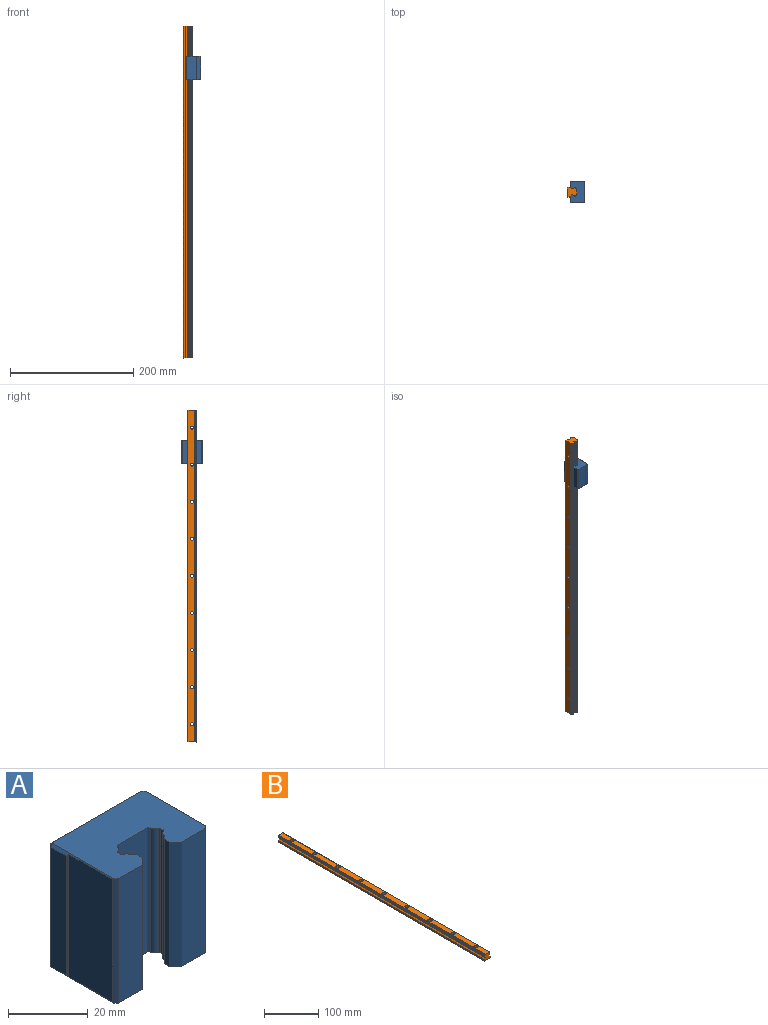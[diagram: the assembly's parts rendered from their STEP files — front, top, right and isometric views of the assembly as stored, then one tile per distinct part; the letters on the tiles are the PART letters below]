
ASSEMBLY  parts=2 mates=1
PART A: 58 faces, bbox 34x23.5x38.2 mm
  f0: plane 3.25x3.25mm, normal (0,1,0), area 8.3mm2, adj f14
  f1: plane 3.25x3.25mm, normal (0,1,0), area 8.3mm2, adj f15
  f2: plane 3.25x3.25mm, normal (0,1,0), area 8.3mm2, adj f18
  f3: plane 3.25x3.25mm, normal (0,1,0), area 8.3mm2, adj f19
  f4: plane 37.7x0.5mm, normal (-0.62,-0.78,0), area 23.8mm2, adj f8,f23,f24,f42
  f5: plane 38.2x0.92mm, normal (1,0,0), area 35.1mm2, adj f26,f28,f34,f57
  f6: plane 38.2x0.92mm, normal (-1,0,0), area 35.1mm2, adj f30,f32,f34,f57
  f7: plane 1.31x1.31mm, normal (-0.5,0.5,-0.71), area 1.2mm2, adj f8,f17,f21,f34
  f8: plane 21.75x0.75mm, normal (-0.71,0,-0.71), area 11.6mm2, adj f4,f7,f23,f24,f25,f34
  f9: plane 1.31x1.31mm, normal (0.5,0.5,-0.71), area 1.2mm2, adj f11,f12,f21,f34
  f10: plane 37.7x0.5mm, normal (0.62,-0.78,0), area 23.8mm2, adj f11,f36,f37,f54
  f11: plane 21.75x0.75mm, normal (0.71,0,-0.71), area 11.6mm2, adj f9,f10,f34,f35,f36,f37
  f12: plane 36.7x1mm, normal (0.71,0.71,0), area 51.9mm2, adj f9,f37,f38,f55
  f13: plane 37.51x0.41mm, normal (-0.71,0.71,0), area 21.4mm2, adj f20,f21,f38,f56
  f14: cylinder r=1.62mm len=15mm, axis (0,-1,0), area 153.2mm2, adj f0,f38
  f15: cylinder r=1.62mm len=15mm, axis (0,-1,0), area 153.2mm2, adj f1,f38
  f16: plane 37.51x0.41mm, normal (0.71,0.71,0), area 21.4mm2, adj f21,f22,f39,f56
  f17: plane 36.7x1mm, normal (-0.71,0.71,0), area 51.9mm2, adj f7,f24,f39,f41
  f18: cylinder r=1.62mm len=15mm, axis (0,-1,0), area 153.2mm2, adj f2,f39
  f19: cylinder r=1.62mm len=15mm, axis (0,-1,0), area 153.2mm2, adj f3,f39
  f20: cylinder r=1mm len=38.1mm, axis (0,0,-1), area 29.8mm2, adj f13,f21,f40,f56
  f21: plane 32x0.75mm, normal (0,0.71,-0.71), area 23mm2, adj f7,f9,f13,f16,f20,f22,f34,f38
  f22: cylinder r=1mm len=38.1mm, axis (0,0,-1), area 29.8mm2, adj f16,f21,f40,f56
  f23: plane 37.7x15.5mm, normal (-1,0,0), area 584.3mm2, adj f4,f8,f25,f42
  f24: plane 36.7x5.6mm, normal (-1,0,0), area 205.5mm2, adj f4,f8,f17,f42
  f25: plane 38.2x1mm, normal (-0.71,-0.71,0), area 53.9mm2, adj f8,f23,f34,f42,f43,f57
  f26: cylinder r=0.5mm len=38.2mm, axis (0,0,-1), area 25mm2, adj f5,f34,f46,f57
  f27: plane 38.2x1.09mm, normal (0.68,0.74,0), area 56.3mm2, adj f34,f45,f46,f57
  f28: cylinder r=0.5mm len=38.2mm, axis (0,0,-1), area 25mm2, adj f5,f34,f47,f57
  f29: plane 38.2x0.5mm, normal (0.71,-0.71,0), area 26.8mm2, adj f34,f47,f48,f57
  f30: cylinder r=0.5mm len=38.2mm, axis (0,0,-1), area 25mm2, adj f6,f34,f49,f57
  f31: plane 38.2x0.5mm, normal (-0.71,-0.71,0), area 26.8mm2, adj f34,f48,f49,f57
  f32: cylinder r=0.5mm len=38.2mm, axis (0,0,-1), area 25mm2, adj f6,f34,f50,f57
  f33: plane 38.2x1.09mm, normal (-0.68,0.74,0), area 56.3mm2, adj f34,f50,f51,f57
  f34: plane 32.5x22.75mm, normal (0,0,-1), area 612.7mm2, adj f5,f6,f7,f8,f9,f11,f21,f25
  f35: plane 38.2x1mm, normal (0.71,-0.71,0), area 53.9mm2, adj f11,f34,f36,f53,f54,f57
  f36: plane 37.7x15.5mm, normal (1,0,0), area 584.3mm2, adj f10,f11,f35,f54
  f37: plane 36.7x5.6mm, normal (1,0,0), area 205.5mm2, adj f10,f11,f12,f54
  f38: plane 36.7x10.25mm, normal (0,1,0), area 359.6mm2, adj f12,f13,f14,f15,f21,f56
  f39: plane 36.7x10.25mm, normal (0,1,0), area 359.6mm2, adj f16,f17,f18,f19,f21,f56
  f40: plane 38.1x9.27mm, normal (0,1,0), area 353.2mm2, adj f20,f21,f22,f56
  f41: plane 1.31x1.31mm, normal (-0.5,0.5,0.71), area 1.2mm2, adj f17,f42,f56,f57
  f42: plane 21.75x0.75mm, normal (-0.71,0,0.71), area 11.6mm2, adj f4,f23,f24,f25,f41,f57
  f43: plane 38.2x8.54mm, normal (0,-1,0), area 326.2mm2, adj f25,f34,f44,f57
  f44: plane 38.2x2.16mm, normal (0.68,-0.73,0), area 112.5mm2, adj f34,f43,f45,f57
  f45: plane 38.2x2mm, normal (1,0,0), area 76.4mm2, adj f27,f34,f44,f57
  f46: cylinder r=1.67mm len=38.2mm, axis (0,0,-1), area 81.4mm2, adj f26,f27,f34,f57
  f47: cylinder r=1.67mm len=38.2mm, axis (0,0,-1), area 81.4mm2, adj f28,f29,f34,f57
  f48: plane 38.2x10.78mm, normal (0,-1,0), area 411.8mm2, adj f29,f31,f34,f57
  f49: cylinder r=1.67mm len=38.2mm, axis (0,0,-1), area 81.4mm2, adj f30,f31,f34,f57
  f50: cylinder r=1.67mm len=38.2mm, axis (0,0,-1), area 81.4mm2, adj f32,f33,f34,f57
  f51: plane 38.2x2mm, normal (-1,0,0), area 76.4mm2, adj f33,f34,f52,f57
  f52: plane 38.2x2.16mm, normal (-0.68,-0.73,0), area 112.5mm2, adj f34,f51,f53,f57
  f53: plane 38.2x8.54mm, normal (0,-1,0), area 326.2mm2, adj f34,f35,f52,f57
  f54: plane 21.75x0.75mm, normal (0.71,0,0.71), area 11.6mm2, adj f10,f35,f36,f37,f55,f57
  f55: plane 1.31x1.31mm, normal (0.5,0.5,0.71), area 1.2mm2, adj f12,f54,f56,f57
  f56: plane 32x0.75mm, normal (0,0.71,0.71), area 23mm2, adj f13,f16,f20,f22,f38,f39,f40,f41
  f57: plane 32.5x22.75mm, normal (0,0,1), area 612.7mm2, adj f5,f6,f25,f26,f27,f28,f29,f30
PART B: 55 faces, bbox 15x538x15 mm
  f0: plane 538x0.92mm, normal (1,0,0), area 496.6mm2, adj f4,f5,f42,f44
  f1: plane 538x0.92mm, normal (-1,0,0), area 496.6mm2, adj f8,f9,f42,f44
  f2: plane 538x1mm, normal (0.71,0,-0.71), area 760.8mm2, adj f20,f21,f42,f44
  f3: plane 538x1.09mm, normal (0.68,0,-0.74), area 796.4mm2, adj f23,f24,f42,f44
  f4: cylinder r=0.45mm len=538mm, axis (0,-1,0), area 317.5mm2, adj f0,f24,f42,f44
  f5: cylinder r=0.45mm len=538mm, axis (0,-1,0), area 317.5mm2, adj f0,f25,f42,f44
  f6: plane 538x0.47mm, normal (0.71,0,0.71), area 358.8mm2, adj f25,f26,f42,f44
  f7: plane 538x0.47mm, normal (-0.71,0,0.71), area 358.8mm2, adj f26,f27,f42,f44
  f8: cylinder r=0.45mm len=538mm, axis (0,-1,0), area 317.5mm2, adj f1,f27,f42,f44
  f9: cylinder r=0.45mm len=538mm, axis (0,-1,0), area 317.5mm2, adj f1,f28,f42,f44
  f10: plane 538x1.09mm, normal (-0.68,0,-0.74), area 796.4mm2, adj f28,f29,f42,f44
  f11: cylinder r=3.75mm len=7.5mm, axis (0,0,-1), area 129.6mm2, adj f26,f32
  f12: cylinder r=3.75mm len=7.5mm, axis (0,0,-1), area 129.6mm2, adj f26,f33
  f13: cylinder r=3.75mm len=7.5mm, axis (0,0,-1), area 129.6mm2, adj f26,f34
  f14: cylinder r=3.75mm len=7.5mm, axis (0,0,-1), area 129.6mm2, adj f26,f35
  f15: cylinder r=3.75mm len=7.5mm, axis (0,0,-1), area 129.6mm2, adj f26,f36
  f16: cylinder r=3.75mm len=7.5mm, axis (0,0,-1), area 129.6mm2, adj f26,f37
  f17: cylinder r=3.75mm len=7.5mm, axis (0,0,-1), area 129.6mm2, adj f26,f38
  f18: cylinder r=3.75mm len=7.5mm, axis (0,0,-1), area 129.6mm2, adj f26,f39
  f19: cylinder r=3.75mm len=7.5mm, axis (0,0,-1), area 129.6mm2, adj f26,f40
  f20: plane 538x0.73mm, normal (0,0,-1), area 390.3mm2, adj f2,f42,f43,f44
  f21: plane 538x3mm, normal (1,0,0), area 1614mm2, adj f2,f22,f42,f44
  f22: plane 538x2.75mm, normal (0.68,0,0.73), area 2016.3mm2, adj f21,f23,f42,f44
  f23: plane 538x1.98mm, normal (1,0,0), area 1062.9mm2, adj f3,f22,f42,f44
  f24: cylinder r=1.72mm len=538mm, axis (0,-1,0), area 1168.9mm2, adj f3,f4,f42,f44
  f25: cylinder r=1.72mm len=538mm, axis (0,-1,0), area 1169.6mm2, adj f5,f6,f42,f44
  f26: plane 538x10.74mm, normal (0,0,1), area 5379.7mm2, adj f6,f7,f11,f12,f13,f14,f15,f16
  f27: cylinder r=1.72mm len=538mm, axis (0,-1,0), area 1169.6mm2, adj f7,f8,f42,f44
  f28: cylinder r=1.72mm len=538mm, axis (0,-1,0), area 1168.9mm2, adj f9,f10,f42,f44
  f29: plane 538x1.98mm, normal (-1,0,0), area 1062.9mm2, adj f10,f30,f42,f44
  f30: plane 538x2.75mm, normal (-0.68,0,0.73), area 2016.3mm2, adj f29,f31,f42,f44
  f31: plane 538x3mm, normal (-1,0,0), area 1614mm2, adj f30,f41,f42,f44
  f32: plane 7.5x7.5mm, normal (0,0,1), area 26.8mm2, adj f11,f45
  f33: plane 7.5x7.5mm, normal (0,0,1), area 26.8mm2, adj f12,f46
  f34: plane 7.5x7.5mm, normal (0,0,1), area 26.8mm2, adj f13,f47
  f35: plane 7.5x7.5mm, normal (0,0,1), area 26.8mm2, adj f14,f48
  f36: plane 7.5x7.5mm, normal (0,0,1), area 26.8mm2, adj f15,f49
  f37: plane 7.5x7.5mm, normal (0,0,1), area 26.8mm2, adj f16,f50
  f38: plane 7.5x7.5mm, normal (0,0,1), area 26.8mm2, adj f17,f51
  f39: plane 7.5x7.5mm, normal (0,0,1), area 26.8mm2, adj f18,f52
  f40: plane 7.5x7.5mm, normal (0,0,1), area 26.8mm2, adj f19,f53
  f41: plane 538x1mm, normal (-0.71,0,-0.71), area 760.8mm2, adj f31,f42,f44,f54
  f42: plane 15x14.95mm, normal (0,-1,0), area 189.9mm2, adj f0,f1,f2,f3,f4,f5,f6,f7
  f43: cylinder r=0.8mm len=538mm, axis (0,-1,0), area 1134.6mm2, adj f20,f42,f44,f54
  f44: plane 15x14.95mm, normal (0,1,0), area 189.9mm2, adj f0,f1,f2,f3,f4,f5,f6,f7
  f45: cylinder r=2.35mm len=9.45mm, axis (0,0,-1), area 139.5mm2, adj f32,f54
  f46: cylinder r=2.35mm len=9.45mm, axis (0,0,-1), area 139.5mm2, adj f33,f54
  f47: cylinder r=2.35mm len=9.45mm, axis (0,0,-1), area 139.5mm2, adj f34,f54
  f48: cylinder r=2.35mm len=9.45mm, axis (0,0,-1), area 139.5mm2, adj f35,f54
  f49: cylinder r=2.35mm len=9.45mm, axis (0,0,-1), area 139.5mm2, adj f36,f54
  f50: cylinder r=2.35mm len=9.45mm, axis (0,0,-1), area 139.5mm2, adj f37,f54
  f51: cylinder r=2.35mm len=9.45mm, axis (0,0,-1), area 139.5mm2, adj f38,f54
  f52: cylinder r=2.35mm len=9.45mm, axis (0,0,-1), area 139.5mm2, adj f39,f54
  f53: cylinder r=2.35mm len=9.45mm, axis (0,0,-1), area 139.5mm2, adj f40,f54
  f54: plane 538x10.73mm, normal (0,0,-1), area 5614.1mm2, adj f41,f42,f43,f44,f45,f46,f47,f48
PLACE A rot(axis=(0,0,-1),90deg) t=(11.95,-1.14,-68.14)mm
PLACE B rot(axis=(-0.58,0.58,-0.58),120deg) t=(0,-1.14,-538)mm
MATE slider B.f42 <-> A.f57  axis (0,0,1) through (14.95,-1.14,0)mm
